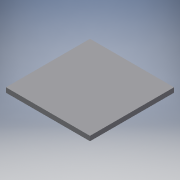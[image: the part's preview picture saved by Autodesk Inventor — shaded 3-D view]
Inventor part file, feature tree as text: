
AUTODESK INVENTOR PART (.ipt)
format: ipt  version: 2018.3 (Build 223284000, 284)  size: 82,944 bytes
history: native  units: mm
features: extrude x1, sketch x1
ambient origin geometry x8: Origin, YZ Plane, XZ Plane, XY Plane, X Axis, Y Axis, Z Axis, Center Point
bodies: Solid1 (feature_tree)
feature tree (2):
  extrude  "Extrusion1"  Depth=36.0mm
  sketch  "Sketch1"  dims[d0=36.0mm d1=36.0mm d2=2.0mm d3=0.0mm]
